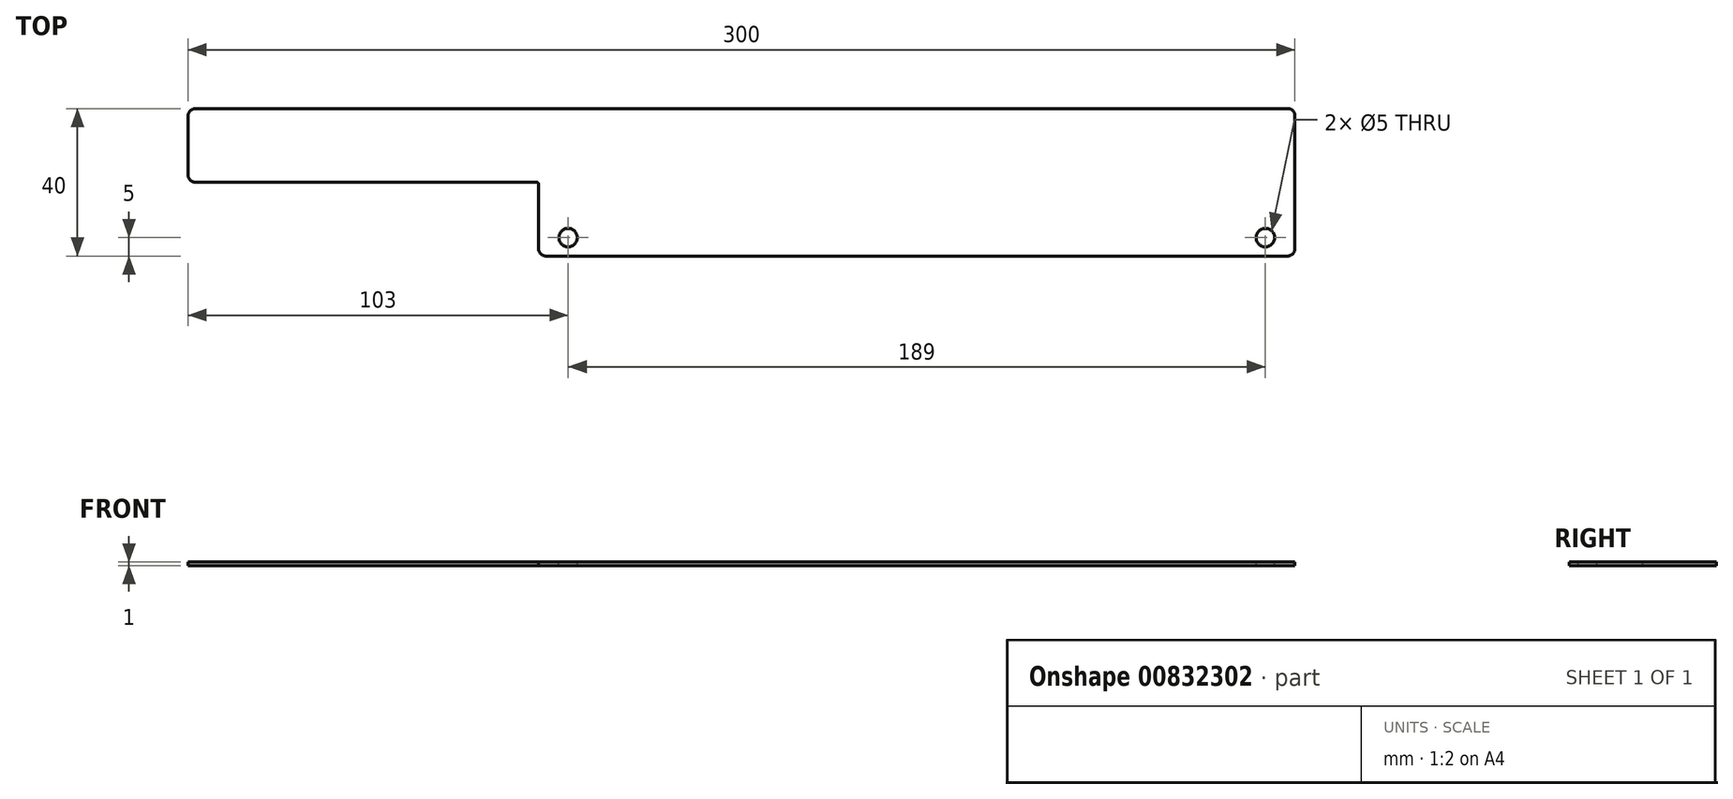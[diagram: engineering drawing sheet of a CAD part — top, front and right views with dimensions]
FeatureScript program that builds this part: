
annotation { "Feature Type Name" : "Feature", "Feature Type Description" : "" }
export const myFeature = defineFeature(function(context is Context, id is Id, definition is map)
    precondition{}
    {
        {
            var Q0;
            Q0=qCreatedBy(makeId("Top.planeOp"),FACE);
            var sketch = newSketch(context, id + "F0", { "sketchPlane" : qUnion([Q0])});
            skLineSegment(sketch, "E0.bottom", {"start": v(0, 0) * mm, "end": v(-300, 0) * mm});
            skLineSegment(sketch, "E0.top", {"start": v(0, -40) * mm, "end": v(-205, -40) * mm});
            skLineSegment(sketch, "E0.left", {"start": v(0, 0) * mm, "end": v(0, -40) * mm});
            skLineSegment(sketch, "E0.right", {"start": v(-300, 0) * mm, "end": v(-300, -20) * mm});
            skLineSegment(sketch, "E1.top", {"start": v(-300, -20) * mm, "end": v(-205, -20) * mm});
            skLineSegment(sketch, "E1.right", {"start": v(-205, -40) * mm, "end": v(-205, -20) * mm});
            skSolve(sketch);
        }
        {
            var Q0;
            Q0=makeQuery(id+"F0.imprint","IMPRINT",FACE,{"disambiguationData":[TD([[makeQuery(id+"F0.imprint","IMPRINT",EDGE,{"derivedFrom":sQuery(id+"F0.wireOp",EDGE,"E0.bottom")}),1.0]])]});
            extrude(context, id + "F1", {"entities" : qUnion([Q0]), "oppositeDirection" : true, "depth" : 1 * mm, "offsetDistance" : 25 * mm});
        }
        {
            var Q0;
            Q0=makeQuery(id+"F1.opExtrude","SWEPT_EDGE",EDGE,{"disambiguationData":[OSD([sQuery(id+"F0.wireOp",EDGE,"E0.right"),sQuery(id+"F0.wireOp",EDGE,"E1.top")])]});
            var Q1;
            Q1=makeQuery(id+"F1.opExtrude","SWEPT_EDGE",EDGE,{"disambiguationData":[OSD([sQuery(id+"F0.wireOp",EDGE,"E0.bottom"),sQuery(id+"F0.wireOp",EDGE,"E0.right")])]});
            var Q2;
            Q2=makeQuery(id+"F1.opExtrude","SWEPT_EDGE",EDGE,{"disambiguationData":[OSD([sQuery(id+"F0.wireOp",EDGE,"E0.top"),sQuery(id+"F0.wireOp",EDGE,"E1.right")])]});
            var Q3;
            Q3=makeQuery(id+"F1.opExtrude","SWEPT_EDGE",EDGE,{"disambiguationData":[OSD([sQuery(id+"F0.wireOp",EDGE,"E0.bottom"),sQuery(id+"F0.wireOp",EDGE,"E0.left")])]});
            var Q4;
            Q4=makeQuery(id+"F1.opExtrude","SWEPT_EDGE",EDGE,{"disambiguationData":[OSD([sQuery(id+"F0.wireOp",EDGE,"E0.top"),sQuery(id+"F0.wireOp",EDGE,"E0.left")])]});
            fillet(context, id + "F2", {"entities" : qUnion([Q0, Q1, Q2, Q3, Q4]), "radius" : 2 * mm, "tangentPropagation" : true, "allowEdgeOverflow" : false});
        }
        {
            var Q0;
            Q0=makeQuery(id+"F1.opExtrude","SWEPT_EDGE",EDGE,{"disambiguationData":[OSD([sQuery(id+"F0.wireOp",EDGE,"E1.top"),sQuery(id+"F0.wireOp",EDGE,"E1.right")])]});
            fillet(context, id + "F3", {"entities" : qUnion([Q0]), "radius" : 0.5 * mm, "tangentPropagation" : true, "allowEdgeOverflow" : false});
        }
        {
            var Q0;
            Q0=makeQuery(id+"F1.opExtrude","CAP_FACE",FACE,{"disambiguationData":[OSD([sQuery(id+"F0.wireOp",EDGE,"E0.bottom"),sQuery(id+"F0.wireOp",EDGE,"E0.top"),sQuery(id+"F0.wireOp",EDGE,"E0.left"),sQuery(id+"F0.wireOp",EDGE,"E0.right"),sQuery(id+"F0.wireOp",EDGE,"E1.top"),sQuery(id+"F0.wireOp",EDGE,"E1.right")])],"isStart":true});
            var sketch = newSketch(context, id + "F4", { "sketchPlane" : qUnion([Q0])});
            skPoint(sketch, "E2", {"position": v(-197, -35) * mm});
            skPoint(sketch, "E3", {"position": v(-8, -35) * mm});
            skSolve(sketch);
        }
        {
            var Q0;
            Q0=sQuery(id+"F4.wireOp",VERTEX,"E2");
            var Q1;
            Q1=sQuery(id+"F4.wireOp",VERTEX,"E3");
            var Q2;
            Q2=makeQuery(id+"F1.opExtrude","SWEPT_BODY",BODY,{"disambiguationData":[OSD([sQuery(id+"F0.wireOp",EDGE,"E0.bottom"),sQuery(id+"F0.wireOp",EDGE,"E0.top"),sQuery(id+"F0.wireOp",EDGE,"E0.left"),sQuery(id+"F0.wireOp",EDGE,"E0.right"),sQuery(id+"F0.wireOp",EDGE,"E1.top"),sQuery(id+"F0.wireOp",EDGE,"E1.right")])]});
            hole(context, id + "F5", {"style" : HoleStyle.SIMPLE, "endStyle" : HoleEndStyle.THROUGH, "holeDiameter" : 5 * mm, "majorDiameter" : 5 * mm, "isTappedThrough" : true, "tappedDepth" : 12 * mm, "tapClearance" : 3, "locations" : qUnion([Q0, Q1]), "scope" : qUnion([Q2])});
        }
    });
